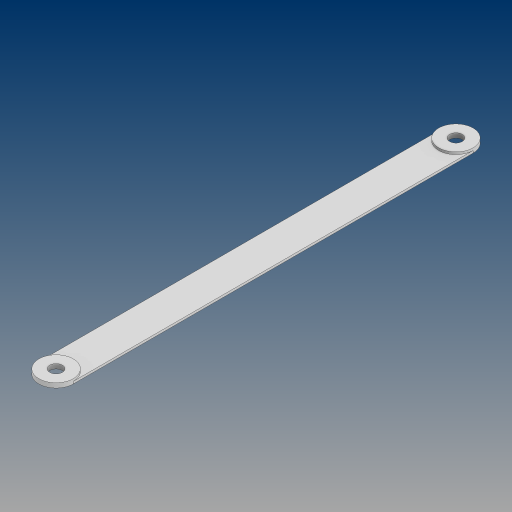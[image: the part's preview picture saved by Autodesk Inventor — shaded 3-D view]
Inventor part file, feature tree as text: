
AUTODESK INVENTOR PART (.ipt)
format: ipt  version: 2023 (Build 270158000, 158)  size: 99,840 bytes
history: native  units: mm
features: extrude x2, sketch x1
ambient origin geometry x8: Origin, YZ Plane, XZ Plane, XY Plane, X Axis, Y Axis, Z Axis, Center Point
bodies: Solid1 (feature_tree)
feature tree (3):
  sketch  "Sketch1"  dims[d0=5.5mm d1=174.842mm d2=90.0deg d3=5.5mm d4=15.0mm d5=2.0mm d6=0.0mm d7=1.0mm d8=0.0mm]
  extrude  "Extrusion1"  Depth=174.842mm
  extrude  "Extrusion2"  TaperAngle=90.0deg  [1 undecoded]
note: 1 required parameter value undecoded (feature->parameter linkage not recoverable at this tier; creation-order binding heuristic only, values carry confidence <= 0.55)
